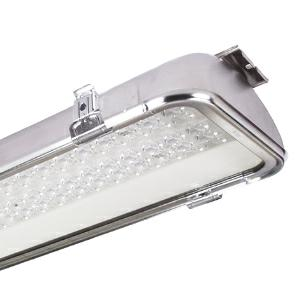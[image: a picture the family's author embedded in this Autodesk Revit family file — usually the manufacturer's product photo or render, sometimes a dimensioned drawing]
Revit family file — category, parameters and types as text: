
# Revit family: 3f_filippi_-_beta_235_93_vt_ampio_3f_filippi_-_52793_-_beta_235_led_931x60_ampio_vt_l1565
name_source: partatom
category: Lighting Fixtures
units: mm (PartAtom-declared; Revit-internal decimal feet)

## family parameters
Cut with Voids When Loaded = No
Host = Face
Light Source = No
Part Type = Normal
Room Calculation Point = No
Round Connector Dimension = Use Diameter
Shared = No

## types (1)
- 3F Filippi - Beta 235 93 VT Ampio (1 x LED, 10287 lm, 65 W, 4000 K)
    Apparent Load = 65 VA
    Approval mark = CE
    CIE Flux Codes = 56 92 99 100 100
    Color Rendering = 80
    Color Temperature = 4000 K
    Control Gear = Electronic ballast
    Default Elevation = 1800 mm
    Description = ILLUMINOTECHNICAL
Luminous efficiency 100% (DLOR 100%, ULOR 0%).
Initial luminous flux of the luminaire 10287 lm.
Wide symmetric distribution.
Installation Interdistance Transv.D = 1.19 x hu - Long.D = 1.18 x hu.
Tabular UGR (CIE 117 - 4H-8H; S=0.25H; 70/50/20): RUG 20.2 - 21.8.
Beam angle: 99° - 105°.
Luminous efficacy 158 lm/W.
Lifetime (L93/B10): 30000 h. (tq+25°C)
Lifetime (L90/B10): 50000 h. (tq+25°C)
Lifetime (L85/B10): 80000 h. (tq+25°C)
Lifetime (L80/B10): 100000 h. (tq+25°C)
Lifetime (L85/B10): 50000 h. (tq+45°C)
Sudden decreased luminous flux after 50000 hours: 0% (C0).
Photobiological safety in compliance with IEC/TR 62778: RG0 risk exempt, (IEC 62471).
In compliance with IEC/EN 62722-2-1 - IEC/EN 62717 standards.

SOURCE
Linear LED module 60W/840.
Energy efficiency class (UE 2019/2020 - UE 2019/2015): C.
CIE 13.3 Colour rendering index: CRI >80 (R9 <50%).
IES TM-30 Fidelity Index: Rf = 84 Rg = 95.
CCT nominal colour temperature 4000 K.
Colour initial tolerance (MacAdam): SDCM 3.

MECHANICAL
Housing in AISI 304 stainless steel, pressed in one single piece.
VT transparent glass, non-combustible, single-piece perimeter frame in stainless steel.
Oversized gear-tray reflector unit in highly reflective white painted hot-galvanised steel.
Methacrylate (PMMA) lenses with external flat surface.
Stainless steel snap-lock clips for diffuser mounting (safety n° 4 per fixture).
Luminaire with limited surface temperature. - D - (EN 60598-2-24)
Dimensions: 1565x235 mm, height 105 mm. Weight 10.535 kg.
IP65 protection degree.
Mechanical strength to impacts IK09 (10 joule).
Glow-wire test resistance 960°C.

ELECTRICAL
Halogen Free electronic wiring 230V-50/60Hz, power factor 0.95, THD <25%, constant output current, class I, 1 driver.
Power of the luminaire 65 W.
ENEC - CE.
Flicker: <4%.
Luminaire compliant with EN 60598-2-22 for power supply from a centralised emergency system CPSS (Central Power Supply System), not incorporated in the luminaire - high risk areas excluded. The default power and flux are 100% in AC and 100% in DC.
Ambient temperature from -20°C to +45°C.
Temperature class T6 max 85°C.
Quick connection via M20 3P connector with 9-13 mm tightening range.
Relative humidity UR: <85%.

INSTALLATION
Ceiling / Suspended / Wall.
All accessories dedicated to this product are available on the Catalog and on our website www.3F-Filippi.com.

APPLICATIONS
Dry, dusty indoor environments, subject to occasional water splashes.
Any environments except the ones where the luminaire materials are unsuitable.
Industrial environments, warehouses, environments where security locks are required on all clips, e.g. prisons (on request).
Environments in which it is necessary a total protection against falling fragments (eg environments with foodstuffs or machines with moving parts or with extreme temperature changes), use luminaires with laminated glass.
Tempered glass is not immune to falling fragments from harmless and caused by shocks or exceptionally derived from the tempering process.

WARNING
Fixture not suitable for cold stores with an ambient temperature <0°C and/or relative humidity >85%.
Luminaire designed for disposal/recycling at end-of-life.
Replaceable (LED only) light source by a professional. Replaceable control gear by a professional.
    Height = 105 mm
    Lamp = 1 x LED
    Lamp Light Flux = 10287 lm
    Lamp Power = 65 W
    Lamp count = 1
    Length = 1565 mm
    Lifetime = 50000 h
    Luminous efficacy = 158 lm/W
    Manufacturer = 3F Filippi
    ModVariant = No
    Model = 3F Filippi - 52793 - Beta 235 LED 931x60 AMPIO VT L1565
    Mounting Place = Ceiling
    Mounting Type = Pendant
    Number of Poles = 1
    OnlyDefault = Yes
    Power Factor = 1
    Product Name = 3F Filippi - Beta 235 93 VT Ampio
    Product group = pendant luminaire
    ProductGroupID = 9
    Protection Class = Protection class I
    Protection Degree = IP 65
    RLX_Detail_Level = 1
    RLX_Emergency_Light_Flux = 0 lm
    RLX_Emergency_Type = 0
    RLX_Emergency_Type_DB = No
    RlxData = <blob elided: 89553 chars, md5=0637540e>
    Socket = socket
    Standby Power = 0 W
    System Light Flux = 10287 lm
    System Power = 65 W
    Type Comments = Product without accessories
    Type Image = 3ffilippi_52793.jpg
    URL = http://relux.com
    VarID = ---
    Voltage = 0 V
    Weight = 0.00 kg
    Width = 235 mm

## geometry (parser evidence)
native form markers: Blend x4, Sweep x10
no freeform markers — native parametric forms only
